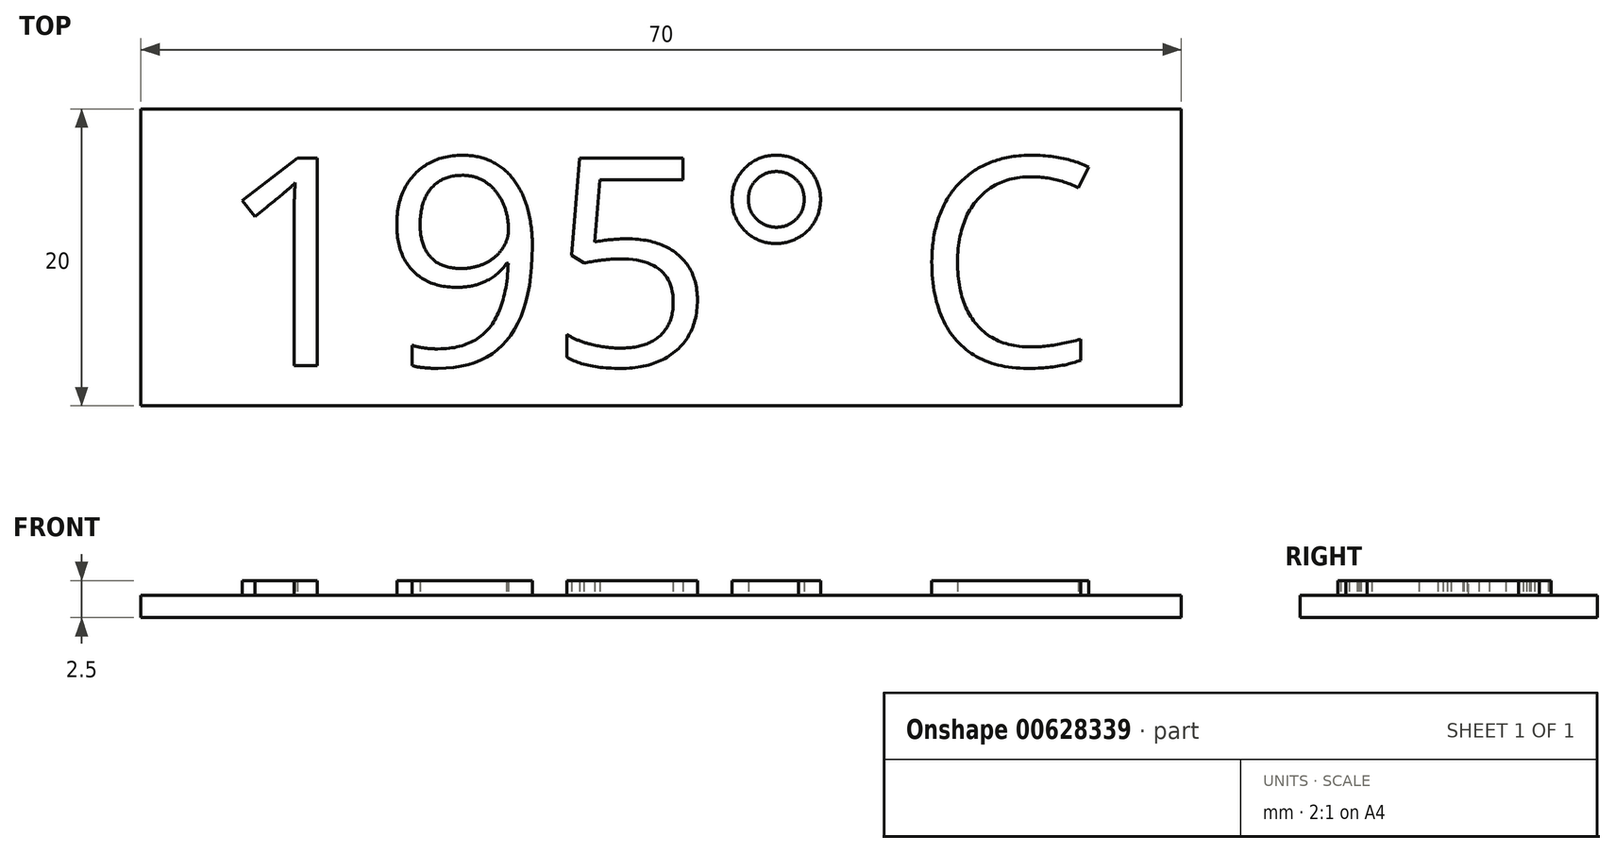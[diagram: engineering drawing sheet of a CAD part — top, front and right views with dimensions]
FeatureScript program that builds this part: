
annotation { "Feature Type Name" : "Feature", "Feature Type Description" : "" }
export const myFeature = defineFeature(function(context is Context, id is Id, definition is map)
    precondition{}
    {
        {
            var Q0;
            Q0=qCreatedBy(makeId("Top.planeOp"),FACE);
            var sketch = newSketch(context, id + "F0", { "sketchPlane" : qUnion([Q0])});
            skLineSegment(sketch, "E0.bottom", {"start": v(-70, 20) * mm, "end": v(0, 20) * mm});
            skLineSegment(sketch, "E0.top", {"start": v(-70, 0) * mm, "end": v(0, 0) * mm});
            skLineSegment(sketch, "E0.left", {"start": v(-70, 20) * mm, "end": v(-70, 0) * mm});
            skLineSegment(sketch, "E0.right", {"start": v(0, 20) * mm, "end": v(0, 0) * mm});
            skSolve(sketch);
        }
        {
            var Q0;
            Q0=makeQuery(id+"F0.imprint","IMPRINT",FACE,{"disambiguationData":[TD([[makeQuery(id+"F0.imprint","IMPRINT",EDGE,{"derivedFrom":sQuery(id+"F0.wireOp",EDGE,"E0.bottom")}),-1.0]])]});
            extrude(context, id + "F1", {"entities" : qUnion([Q0]), "depth" : 1.5 * mm, "offsetDistance" : 25 * mm});
        }
        {
            var Q0;
            Q0=makeQuery(id+"F1.opExtrude","CAP_FACE",FACE,{"disambiguationData":[OSD([sQuery(id+"F0.wireOp",EDGE,"E0.bottom"),sQuery(id+"F0.wireOp",EDGE,"E0.top"),sQuery(id+"F0.wireOp",EDGE,"E0.left"),sQuery(id+"F0.wireOp",EDGE,"E0.right")])],"isStart":false});
            var sketch = newSketch(context, id + "F2", { "sketchPlane" : qUnion([Q0])});
            skText(sketch, "E1", { "text": "195° C", "fontName": "OpenSans-Regular.ttf"});
            const initialGuessF2  = {"E1": [-0.06498, 0.00272, 1, 0, 0.01408]};
            skSetInitialGuess(sketch, initialGuessF2);
            skSolve(sketch);
        }
        {
            var Q0;
            Q0 = qSketchRegion(id + "F2", true);
            extrude(context, id + "F3", {"entities" : qUnion([Q0]), "operationType" : NewBodyOperationType.ADD, "depth" : 1 * mm, "offsetDistance" : 25 * mm});
        }
    });
